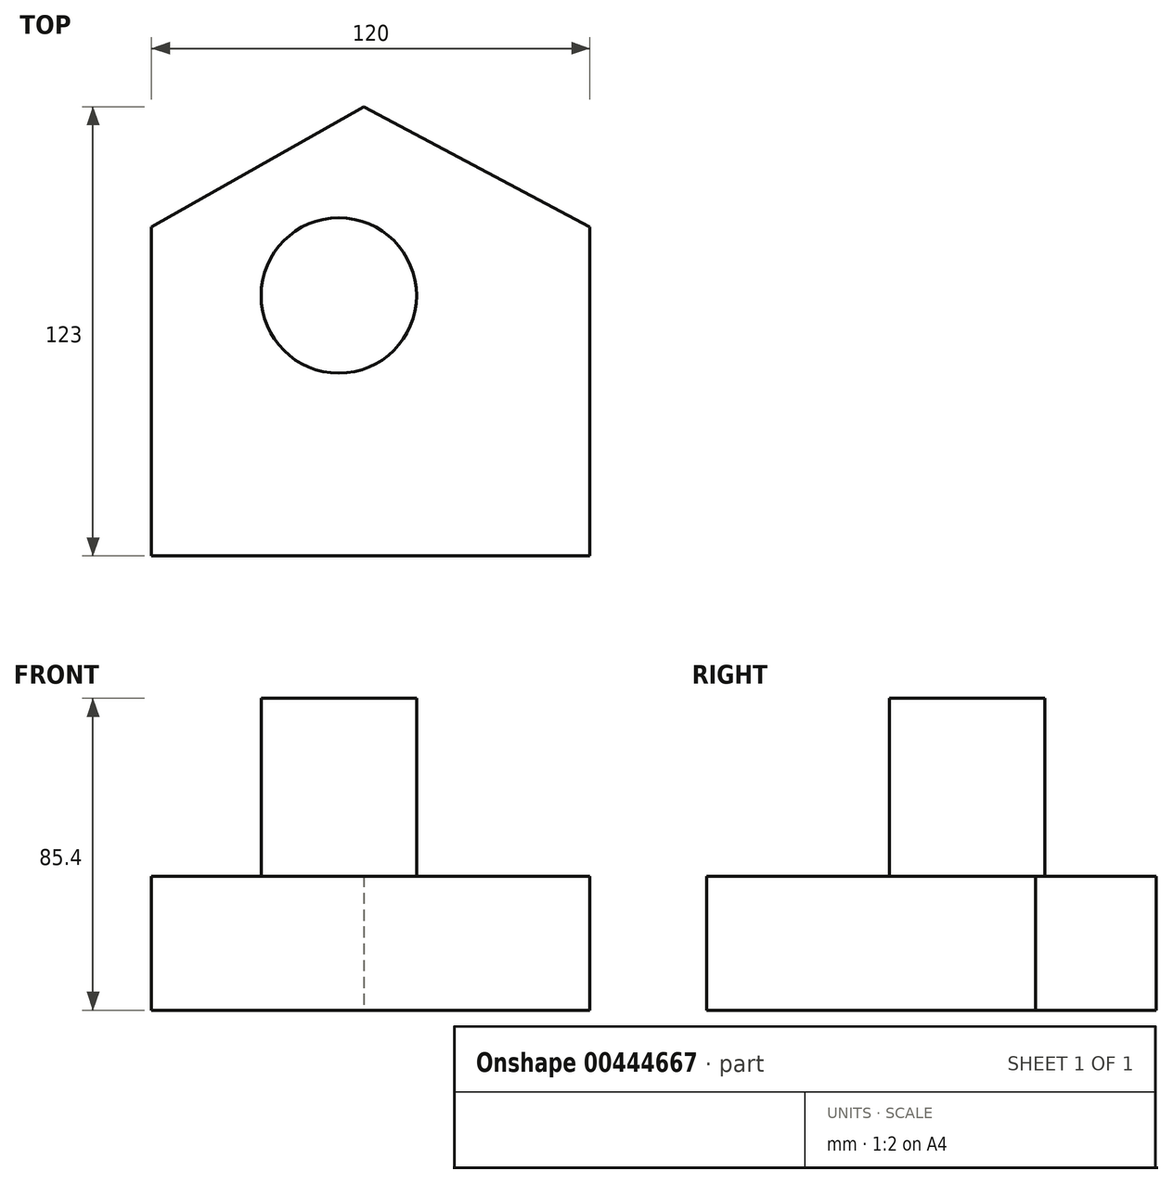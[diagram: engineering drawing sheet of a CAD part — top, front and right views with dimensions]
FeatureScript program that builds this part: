
annotation { "Feature Type Name" : "Feature", "Feature Type Description" : "" }
export const myFeature = defineFeature(function(context is Context, id is Id, definition is map)
    precondition{}
    {
        {
            var Q0;
            Q0=qCreatedBy(makeId("Top.planeOp"),FACE);
            var sketch = newSketch(context, id + "F0", { "sketchPlane" : qUnion([Q0])});
            skLineSegment(sketch, "E0.bottom", {"start": v(-55.46, 18.72) * mm, "end": v(64.54, 18.72) * mm});
            skLineSegment(sketch, "E0.top", {"start": v(-55.46, -71.28) * mm, "end": v(64.54, -71.28) * mm});
            skLineSegment(sketch, "E0.left", {"start": v(-55.46, 18.72) * mm, "end": v(-55.46, -71.28) * mm});
            skLineSegment(sketch, "E0.right", {"start": v(64.54, 18.72) * mm, "end": v(64.54, -71.28) * mm});
            skLineSegment(sketch, "E1", {"start": v(-55.46, 18.72) * mm, "end": v(2.73, 51.72) * mm});
            skLineSegment(sketch, "E2", {"start": v(2.73, 51.72) * mm, "end": v(64.54, 18.72) * mm});
            skSolve(sketch);
        }
        {
            var Q0;
            Q0=makeQuery(id+"F0.imprint","IMPRINT",FACE,{"disambiguationData":[TD([[makeQuery(id+"F0.imprint","IMPRINT",EDGE,{"derivedFrom":sQuery(id+"F0.wireOp",EDGE,"E0.bottom")}),-1.0]])]});
            var Q1;
            Q1=makeQuery(id+"F0.imprint","IMPRINT",FACE,{"disambiguationData":[TD([[makeQuery(id+"F0.imprint","IMPRINT",EDGE,{"derivedFrom":sQuery(id+"F0.wireOp",EDGE,"E0.bottom")}),1.0]])]});
            extrude(context, id + "F1", {"entities" : qUnion([Q0, Q1]), "depth" : 36.7 * mm});
        }
        {
            var Q0;
            Q0=makeQuery(id+"F1.opExtrude","CAP_FACE",FACE,{"disambiguationData":[OSD([sQuery(id+"F0.wireOp",EDGE,"E0.top"),sQuery(id+"F0.wireOp",EDGE,"E0.left"),sQuery(id+"F0.wireOp",EDGE,"E0.right"),sQuery(id+"F0.wireOp",EDGE,"E1"),sQuery(id+"F0.wireOp",EDGE,"E2")])],"isStart":false});
            var sketch = newSketch(context, id + "F2", { "sketchPlane" : qUnion([Q0])});
            skCircle(sketch, "E3", {"center": v(-4.18, 0) * mm, "radius": 21.28 * mm});
            skSolve(sketch);
        }
        {
            var Q0;
            Q0 = qSketchRegion(id + "F2", true);
            extrude(context, id + "F3", {"entities" : qUnion([Q0]), "operationType" : NewBodyOperationType.ADD, "depth" : 48.7 * mm});
        }
    });
